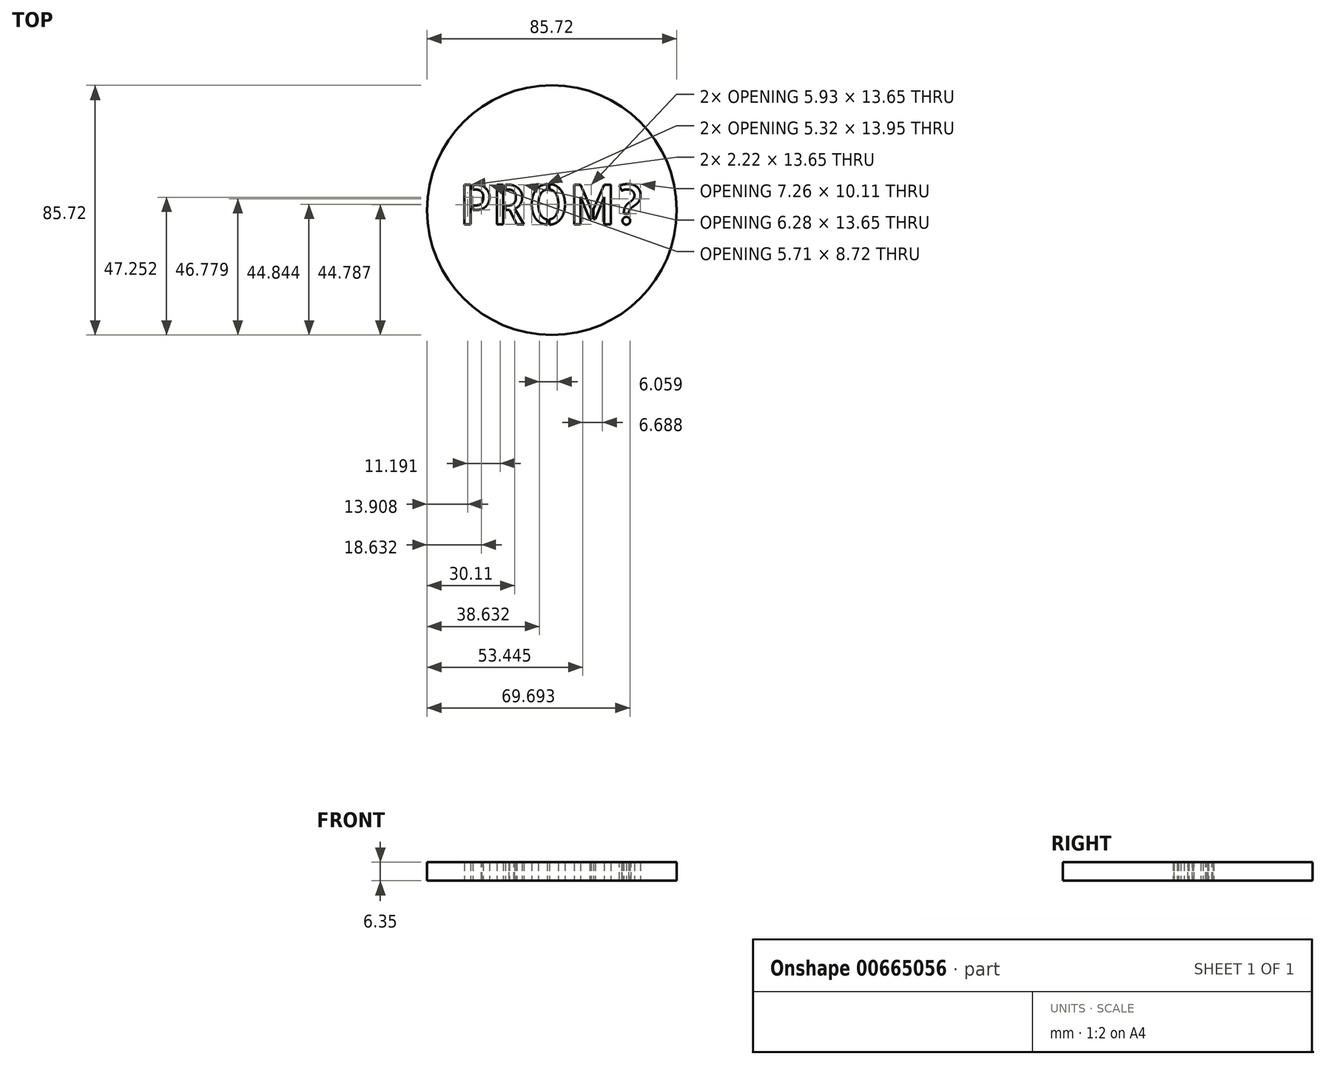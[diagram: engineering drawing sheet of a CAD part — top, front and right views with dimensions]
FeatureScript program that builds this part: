
annotation { "Feature Type Name" : "Feature", "Feature Type Description" : "" }
export const myFeature = defineFeature(function(context is Context, id is Id, definition is map)
    precondition{}
    {
        {
            var Q0;
            Q0=qCreatedBy(makeId("Top.planeOp"),FACE);
            var sketch = newSketch(context, id + "F0", { "sketchPlane" : qUnion([Q0])});
            skCircle(sketch, "E0", {"center": v(0, 0) * mm, "radius": 42.86 * mm});
            skText(sketch, "E1", { "text": "PROM?", "fontName": "AllertaStencil-Regular.ttf"});
            const initialGuessF0  = {"E1": [-0.03175, -0.0049, 1, 0, 0.01366]};
            skSetInitialGuess(sketch, initialGuessF0);
            skSolve(sketch);
        }
        {
            var Q0;
            Q0=makeQuery(id+"F0.imprint","IMPRINT",FACE,{"disambiguationData":[TD([[makeQuery(id+"F0.imprint","IMPRINT",EDGE,{"derivedFrom":sQuery(id+"F0.wireOp",EDGE,"E0")}),1.0]])]});
            extrude(context, id + "F1", {"entities" : qUnion([Q0]), "depth" : 6.35 * mm, "offsetDistance" : 25.4 * mm});
        }
    });
